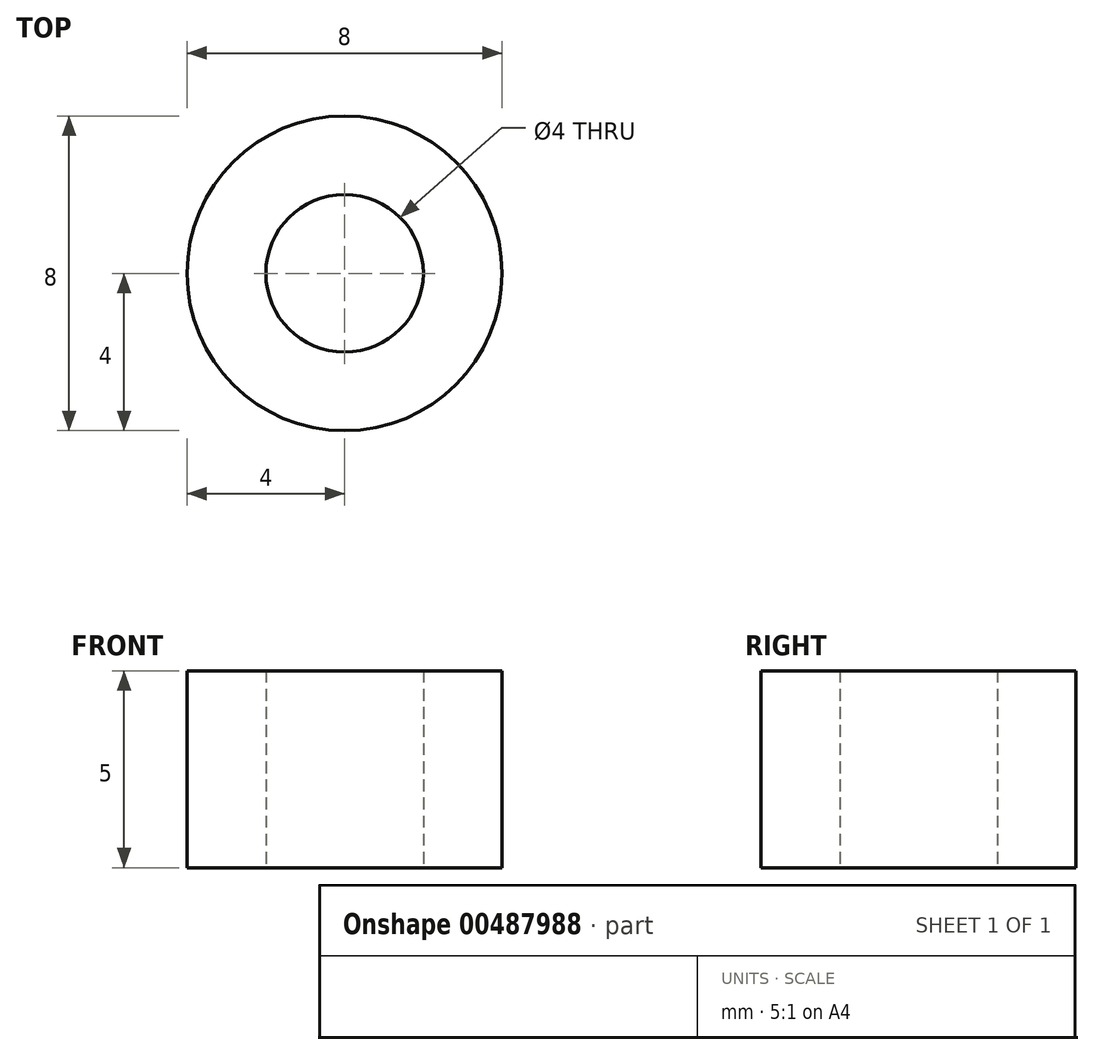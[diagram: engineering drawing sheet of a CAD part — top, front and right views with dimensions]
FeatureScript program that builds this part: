
annotation { "Feature Type Name" : "Feature", "Feature Type Description" : "" }
export const myFeature = defineFeature(function(context is Context, id is Id, definition is map)
    precondition{}
    {
        {
            var Q0;
            Q0=qCreatedBy(makeId("Top.planeOp"),FACE);
            var sketch = newSketch(context, id + "F0", { "sketchPlane" : qUnion([Q0])});
            skCircle(sketch, "E0", {"center": v(0, 0) * mm, "radius": 2 * mm});
            skCircle(sketch, "E1", {"center": v(0, 0) * mm, "radius": 4 * mm});
            skSolve(sketch);
        }
        {
            var Q0;
            Q0=makeQuery(id+"F0.imprint","IMPRINT",FACE,{"disambiguationData":[TD([[makeQuery(id+"F0.imprint","IMPRINT",EDGE,{"derivedFrom":sQuery(id+"F0.wireOp",EDGE,"E0")}),-1.0]])]});
            extrude(context, id + "F1", {"entities" : qUnion([Q0]), "depth" : 5 * mm});
        }
    });
